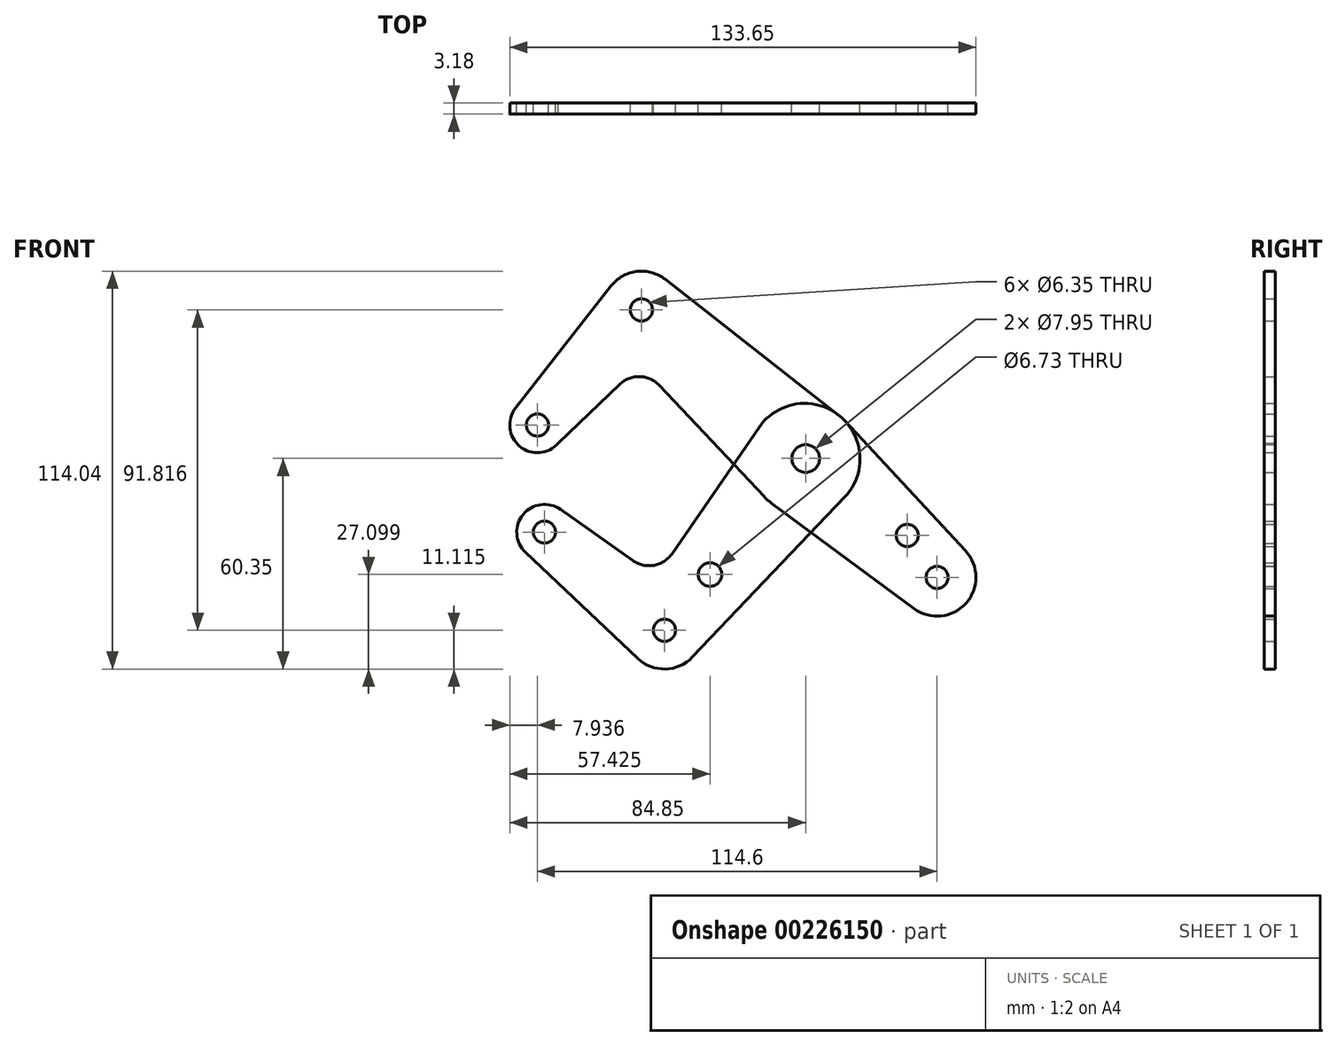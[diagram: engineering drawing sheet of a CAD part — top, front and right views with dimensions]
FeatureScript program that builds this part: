
annotation { "Feature Type Name" : "Feature", "Feature Type Description" : "" }
export const myFeature = defineFeature(function(context is Context, id is Id, definition is map)
    precondition{}
    {
        {
            var Q0;
            Q0=qCreatedBy(makeId("Front.planeOp"),FACE);
            var sketch = newSketch(context, id + "F0", { "sketchPlane" : qUnion([Q0])});
            skLineSegment(sketch, "E0", {"start": v(0, 0) * mm, "end": v(-47.1, 42.58) * mm, "construction": true});
            skLineSegment(sketch, "E1", {"start": v(-47.1, 42.58) * mm, "end": v(-76.91, 9.6) * mm, "construction": true});
            skLineSegment(sketch, "E2", {"start": v(0, 0) * mm, "end": v(37.69, -34.06) * mm, "construction": true});
            skCircle(sketch, "E3", {"center": v(37.69, -34.06) * mm, "radius": 11.11 * mm});
            skCircle(sketch, "E4", {"center": v(-47.1, 42.58) * mm, "radius": 11.11 * mm});
            skCircle(sketch, "E5", {"center": v(-76.91, 9.6) * mm, "radius": 7.94 * mm});
            skCircle(sketch, "E6", {"center": v(-76.91, 9.6) * mm, "radius": 3.18 * mm});
            skCircle(sketch, "E7", {"center": v(-47.1, 42.58) * mm, "radius": 3.18 * mm});
            skCircle(sketch, "E8", {"center": v(0, 0) * mm, "radius": 3.18 * mm});
            skCircle(sketch, "E9", {"center": v(37.69, -34.06) * mm, "radius": 3.18 * mm});
            skCircle(sketch, "E10", {"center": v(29.12, -22.04) * mm, "radius": 3.18 * mm});
            skCircle(sketch, "E11", {"center": v(0, 0) * mm, "radius": 3.98 * mm});
            skLineSegment(sketch, "E12", {"start": v(-55.86, 49.43) * mm, "end": v(-83.17, 14.5) * mm});
            skCircle(sketch, "E13", {"center": v(-0.3, -0.08) * mm, "radius": 15.88 * mm});
            skLineSegment(sketch, "E14", {"start": v(-0.3, -0.08) * mm, "end": v(-40.5, -49.23) * mm, "construction": true});
            skLineSegment(sketch, "E15", {"start": v(-40.5, -49.23) * mm, "end": v(-74.9, -21.1) * mm, "construction": true});
            skCircle(sketch, "E16", {"center": v(-40.5, -49.23) * mm, "radius": 11.11 * mm});
            skCircle(sketch, "E17", {"center": v(-27.42, -33.25) * mm, "radius": 3.37 * mm});
            skCircle(sketch, "E18", {"center": v(-74.9, -21.1) * mm, "radius": 7.94 * mm});
            skLineSegment(sketch, "E19", {"start": v(-13.36, 8.93) * mm, "end": v(-38.38, -27.3) * mm});
            skLineSegment(sketch, "E20", {"start": v(-32.45, -56.9) * mm, "end": v(11.2, -11.03) * mm});
            skLineSegment(sketch, "E21", {"start": v(-70.33, -14.6) * mm, "end": v(-49.5, -29.29) * mm});
            skLineSegment(sketch, "E22", {"start": v(-80.36, -26.86) * mm, "end": v(-48.13, -57.31) * mm});
            skArc(sketch, "E23.filletArc", {"start": v(-49.5, -29.29) * mm, "mid": v(-43.53, -30.62) * mm, "end": v(-38.38, -27.3) * mm});
            skLineSegment(sketch, "E24", {"start": v(-70.92, 4.4) * mm, "end": v(-53.3, 21.28) * mm});
            skLineSegment(sketch, "E25", {"start": v(-40.26, 51.33) * mm, "end": v(9.49, 12.42) * mm});
            skLineSegment(sketch, "E26", {"start": v(-55.19, 34.95) * mm, "end": v(-54.58, 34.31) * mm});
            skLineSegment(sketch, "E27", {"start": v(11.35, 10.7) * mm, "end": v(45.84, -26.51) * mm});
            skLineSegment(sketch, "E28", {"start": v(-9.73, -12.85) * mm, "end": v(31.08, -43) * mm});
            skLineSegment(sketch, "E29.trimOffspring", {"start": v(-42.01, 21) * mm, "end": v(-11.84, -10.98) * mm});
            skArc(sketch, "E30.filletArc", {"start": v(-42.01, 21) * mm, "mid": v(-47.6, 23.48) * mm, "end": v(-53.3, 21.28) * mm});
            skCircle(sketch, "E31", {"center": v(-74.9, -21.1) * mm, "radius": 3.18 * mm});
            skCircle(sketch, "E32", {"center": v(-40.5, -49.23) * mm, "radius": 3.18 * mm});
            skSolve(sketch);
        }
        {
            var Q0;
            Q0=makeQuery(id+"F0.imprint","IMPRINT",FACE,{"disambiguationData":[TD([[makeQuery(id+"F0.imprint","IMPRINT",EDGE,{"derivedFrom":sQuery(id+"F0.wireOp",EDGE,"E9")}),-1.0]])]});
            var Q1;
            Q1=makeQuery(id+"F0.imprint","IMPRINT",FACE,{"disambiguationData":[TD([[makeQuery(id+"F0.imprint","IMPRINT",EDGE,{"derivedFrom":sQuery(id+"F0.wireOp",EDGE,"E7")}),-1.0]])]});
            var Q2;
            Q2=makeQuery(id+"F0.imprint","IMPRINT",FACE,{"disambiguationData":[TD([[makeQuery(id+"F0.imprint","IMPRINT",EDGE,{"derivedFrom":sQuery(id+"F0.wireOp",EDGE,"E6")}),-1.0]])]});
            var Q3;
            Q3=makeQuery(id+"F0.imprint","IMPRINT",FACE,{"disambiguationData":[TD([[makeQuery(id+"F0.imprint","IMPRINT",EDGE,{"derivedFrom":sQuery(id+"F0.wireOp",EDGE,"E10")}),-1.0]])]});
            var Q4;
            {var subQ0=sQuery(id+"F0.wireOp",EDGE,"E12");Q4=makeQuery(id+"F0.imprint","IMPRINT",FACE,{"disambiguationData":[TD([[makeQuery(id+"F0.imprint","IMPRINT",EDGE,{"derivedFrom":subQ0}),1.0]])]});}
            var Q5;
            Q5=makeQuery(id+"F0.imprint","IMPRINT",FACE,{"disambiguationData":[TD([[makeQuery(id+"F0.imprint","IMPRINT",EDGE,{"derivedFrom":sQuery(id+"F0.wireOp",EDGE,"E11")}),-1.0]])]});
            var Q6;
            {var subQ0=sQuery(id+"F0.wireOp",EDGE,"E19");var subQ1=sQuery(id+"F0.wireOp",EDGE,"E13");var subQ2=makeQuery(id+"F0.imprint","INTERSECT",VERTEX,{"derivedFrom":[subQ1,subQ0]});Q6=makeQuery(id+"F0.imprint","IMPRINT",FACE,{"disambiguationData":[TD([[makeQuery(id+"F0.imprint","IMPRINT",EDGE,{"disambiguationData":[TD([[subQ2,-1.0]])],"derivedFrom":subQ1}),-1.0]])]});}
            var Q7;
            {var subQ0=sQuery(id+"F0.wireOp",EDGE,"E20");var subQ1=sQuery(id+"F0.wireOp",EDGE,"E13");var subQ2=makeQuery(id+"F0.imprint","INTERSECT",VERTEX,{"derivedFrom":[subQ1,subQ0]});Q7=makeQuery(id+"F0.imprint","IMPRINT",FACE,{"disambiguationData":[TD([[makeQuery(id+"F0.imprint","IMPRINT",EDGE,{"disambiguationData":[TD([[subQ2,1.0]])],"derivedFrom":subQ1}),-1.0]])]});}
            extrude(context, id + "F1", {"entities" : qUnion([Q0, Q1, Q2, Q3, Q4, Q5, Q6, Q7]), "depth" : 3.17 * mm});
        }
        {
            var Q0;
            Q0=makeQuery(id+"F0.imprint","IMPRINT",FACE,{"disambiguationData":[TD([[makeQuery(id+"F0.imprint","IMPRINT",EDGE,{"derivedFrom":sQuery(id+"F0.wireOp",EDGE,"E17")}),-1.0]])]});
            var Q1;
            Q1=makeQuery(id+"F0.imprint","IMPRINT",FACE,{"disambiguationData":[TD([[makeQuery(id+"F0.imprint","IMPRINT",EDGE,{"derivedFrom":sQuery(id+"F0.wireOp",EDGE,"E32")}),-1.0]])]});
            var Q2;
            Q2=makeQuery(id+"F0.imprint","IMPRINT",FACE,{"disambiguationData":[TD([[makeQuery(id+"F0.imprint","IMPRINT",EDGE,{"derivedFrom":sQuery(id+"F0.wireOp",EDGE,"E31")}),-1.0]])]});
            var Q3;
            Q3=makeQuery(id+"F0.imprint","IMPRINT",FACE,{"disambiguationData":[TD([[makeQuery(id+"F0.imprint","IMPRINT",EDGE,{"derivedFrom":sQuery(id+"F0.wireOp",EDGE,"E11")}),-1.0]])]});
            var Q4;
            {var subQ0=sQuery(id+"F0.wireOp",EDGE,"E19");var subQ1=sQuery(id+"F0.wireOp",EDGE,"E13");var subQ2=makeQuery(id+"F0.imprint","INTERSECT",VERTEX,{"derivedFrom":[subQ1,subQ0]});Q4=makeQuery(id+"F0.imprint","IMPRINT",FACE,{"disambiguationData":[TD([[makeQuery(id+"F0.imprint","IMPRINT",EDGE,{"disambiguationData":[TD([[subQ2,-1.0]])],"derivedFrom":subQ1}),-1.0]])]});}
            var Q5;
            {var subQ0=sQuery(id+"F0.wireOp",EDGE,"E20");var subQ1=sQuery(id+"F0.wireOp",EDGE,"E13");var subQ2=makeQuery(id+"F0.imprint","INTERSECT",VERTEX,{"derivedFrom":[subQ1,subQ0]});Q5=makeQuery(id+"F0.imprint","IMPRINT",FACE,{"disambiguationData":[TD([[makeQuery(id+"F0.imprint","IMPRINT",EDGE,{"disambiguationData":[TD([[subQ2,1.0]])],"derivedFrom":subQ1}),-1.0]])]});}
            extrude(context, id + "F2", {"entities" : qUnion([Q0, Q1, Q2, Q3, Q4, Q5]), "depth" : 3.17 * mm});
        }
    });
